# Revit family: HDL206NE
name_source: partatom
category: Lighting Fixtures
revit_build: Autodesk Revit 2014 (Build: 20130308_1515(x64)
units: mm (PartAtom-declared; Revit-internal decimal feet)

## types (1)
- HDL206NE
    Apparent Load = 65 VA
    Assembly Code = D5020200
    Color Filter = 16777215
    Connector Description = Lighting Connector
    Default Elevation = 1219.2 mm  [stored 4 ft]
    Description = HDL206NE LED modular flood light ensures a penetrating white light at its output without any light degradation at low temperatures. It offers instant start and restrike. Added features include Low cost of installation, operation and maintenance.
    Dimming Lamp Color Temperature Shift = <None>
    Emit Shape Visible in Rendering = No
    Emit from Rectangle Length = 180 mm  [stored 0.590551 ft]
    Emit from Rectangle Width = 250 mm  [stored 0.82021 ft]
    Features = Battery backup power provides 3 hours at 50% illumination, 90 minutes at full illumination.
Modular construction allows the modules to be supplied interlinked with each other to provide greater light output.
Can be used as a single unit – small floodlight or bulkhead or linked together to replicate a large 250W/400W floodlight.
Can be supplied in multiple configurations of standard or emergency modules.
Integrated power supply.
Low power consumption.
Rugged construction – resistant to vibration.
Independently photometrically tested.
All units supplied with 2 cable entries. Additional entries available on request.
IP66 and IP67.
Optional wire guard available for extra protection.
Narrow, Medium, Wide and Extra wide beam light output available.
Multiple mounting options available.
    Fixture distribution = Direct
    Glass = Hubbell - Glass
    Height = 535 mm
    Housing Material = Paint - Hubbell - Light Silver
    IP Rating = IP66/67
    Lamp = LED
    Length = 265 mm  [stored 0.869423 ft]
    Load Classification = Lighting
    Manufacturer = Chalmit
    Model = HDL206NE
    Mounting = Paint - Hubbell - Light Silver
    Photometric Web File = HDL206NEEEMWx04.ies
    Power Factor = 1
    Product Documentation Link = https://hubbellcdn.com
    Product Link = https://www.hubbell.com
    Reflector Finish = Hubbell - White Glass
    Tilt Angle = 90.00°
    URL = https://www.hubbell.com
    Voltage = 120 V
    Warranty = 5 years Warranty
    Wattage Comments = 65W
    Watts = 65 W
    Width = 280 mm
    Wings = Paint - Hubbell - Light Silver

note: [stored X ft] marks values corroborated as IEEE doubles in the binary element streams (Revit-internal decimal feet)

## geometry (parser evidence)
native form markers: Sweep x4
no freeform markers — native parametric forms only
